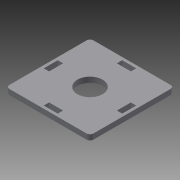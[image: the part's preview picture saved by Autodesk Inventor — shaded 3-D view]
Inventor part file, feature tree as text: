
AUTODESK INVENTOR PART (.ipt)
format: ipt  version: 2015 SP1 (Build 190203100, 203)  size: 121,344 bytes
history: native  units: in
note: dims shown in document units (in); Inventor stores cm internally (conversion verified against a paired STEP export)
features: extrude x1, fillet x1, sketch x1
ambient origin geometry x8: Origin, YZ Plane, XZ Plane, XY Plane, X Axis, Y Axis, Z Axis, Center Point
bodies: Body1 (feature_tree)
feature tree (3):
  extrude  "Extrusion3"  Depth=3.0in
  fillet  "Fillet1"  Radius=1.25in
  sketch  "Sketch1"  dims[d0=3.0in d1=3.0in d6=1.25in d7=0.1in d8=0.19in d9=0.5in d15=1.25in d16=0.5in d17=0.19in d18=0.9in d19=0.19in d20=0.0in d21=0.125in]
